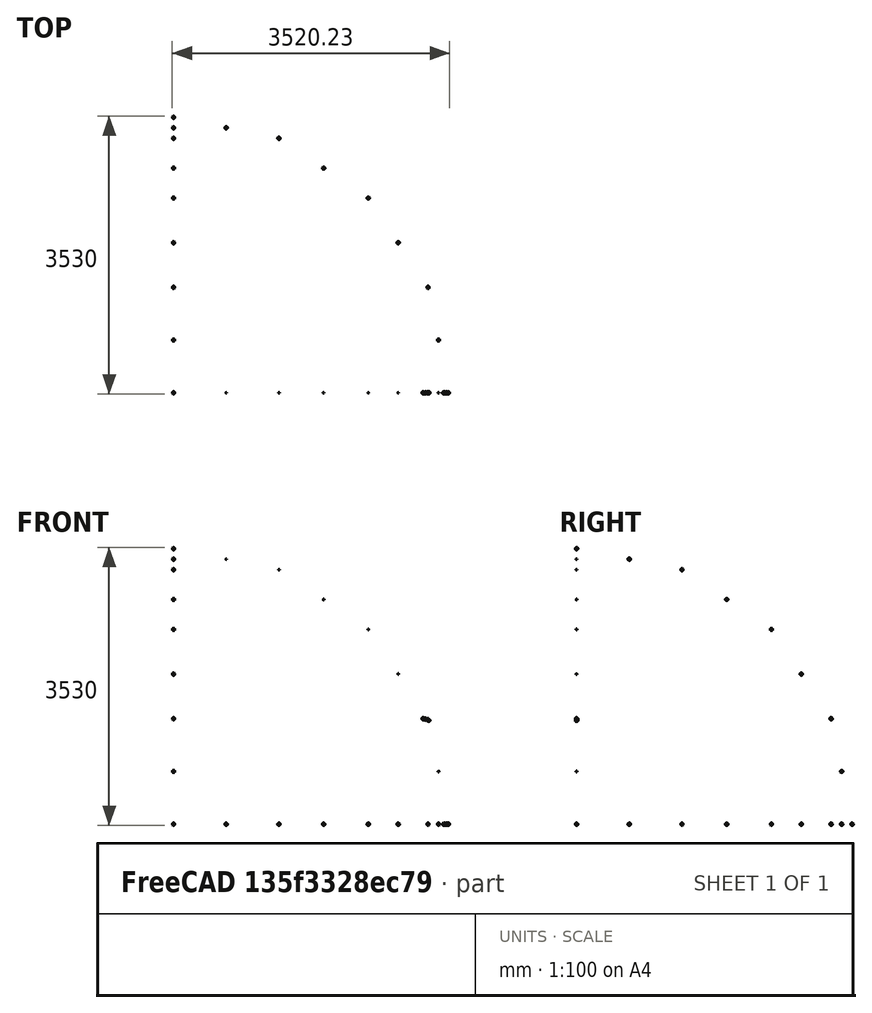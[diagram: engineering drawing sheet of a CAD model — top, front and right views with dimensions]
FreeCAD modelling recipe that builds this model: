
FCSTD DOCUMENT  (FreeCAD 0.20R29603 (Git))
Label: f_pointing
License: All rights reserved
LicenseURL: http://en.wikipedia.org/wiki/All_rights_reserved
objects: Part::Sphere×33, Part::Part2DObjectPython×29, Part::RuledSurface×4
note: 66 computed .brp shape members not serialized (recipe doc carries the construction recipe); baked Part::Feature solids carry a one-line shape summary decoded from their .brp

FEATURE [Part::Part2DObjectPython] Line  # Draft 2D object (typed FeaturePython)
  Area = 0
  ChamferSize = 0
  Closed = false
  End = (3233.58,0,1339.39)
  FilletRadius = 0
  Length = 1365.63
  MakeFace = false
  Points = (2) [(3500,0,0),(3233.58,0,1339.39)]
  Start = (3500,0,0)
  Subdivisions = 0
FEATURE [Part::Part2DObjectPython] Line002  # Draft 2D object (typed FeaturePython)
  Area = 0
  ChamferSize = 0
  Closed = false
  End = (3233.58,1339.39,0)
  FilletRadius = 0
  Length = 1365.63
  MakeFace = false
  Points = (2) [(3500,0,0),(3233.58,1339.39,0)]
  Start = (3500,0,0)
  Subdivisions = 0
FEATURE [Part::Part2DObjectPython] Line003  # Draft 2D object (typed FeaturePython)
  Area = 0
  ChamferSize = 0
  Closed = false
  End = (3171.45,630.84,1339.39)
  FilletRadius = 0
  Length = 1261.68
  MakeFace = false
  Placement = pos=(0,0,0) rot=(0,0,-1;0.19635rad)
  Points = (2) [(3233.58,0,1339.39),(2987.44,1237.44,1339.39)]
  Start = (3171.45,-630.84,1339.39)
  Subdivisions = 0
FEATURE [Part::Part2DObjectPython] Line006  # Draft 2D object (typed FeaturePython)
  Area = 0
  ChamferSize = 0
  Closed = false
  End = (0.0092388,0.00382683,3500)
  FilletRadius = 0
  Length = 0.00390181
  MakeFace = false
  Points = (2) [(0.01,0,3500),(0.0092388,0.00382683,3500)]
  Start = (0.01,0,3500)
  Subdivisions = 0
FEATURE [Part::Part2DObjectPython] Line007  # Draft 2D object (typed FeaturePython)
  Area = 0
  ChamferSize = 0
  Closed = false
  End = (2474.87,0,2474.87)
  FilletRadius = 0
  Length = 1365.63
  MakeFace = false
  Placement = pos=(0,0,0) rot=(0,-1,0;0.392699rad)
  Points = (2) [(3500,0,2.27374e-13),(3233.58,0,1339.39)]
  Start = (3233.58,0,1339.39)
  Subdivisions = 0
FEATURE [Part::Part2DObjectPython] Line008  # Draft 2D object (typed FeaturePython)
  Area = 0
  ChamferSize = 0
  Closed = false
  End = (-1.3642e-12,0,3500)
  FilletRadius = 0
  Length = 1365.63
  MakeFace = false
  Placement = pos=(0,0,0) rot=(0,-1,0;1.1781rad)
  Points = (2) [(3500,0,-4.54747e-13),(3233.58,0,1339.39)]
  Start = (1339.39,0,3233.58)
  Subdivisions = 0
FEATURE [Part::Part2DObjectPython] Line009  # Draft 2D object (typed FeaturePython)
  Area = 0
  ChamferSize = 0
  Closed = false
  End = (1339.39,0,3233.58)
  FilletRadius = 0
  Length = 1365.63
  MakeFace = false
  Placement = pos=(0,0,0) rot=(0,-1,0;0.785398rad)
  Points = (2) [(3500,0,-9.09495e-13),(3233.58,0,1339.39)]
  Start = (2474.87,0,2474.87)
  Subdivisions = 0
FEATURE [Part::Part2DObjectPython] Line010  # Draft 2D object (typed FeaturePython)
  Area = 0
  ChamferSize = 0
  Closed = false
  End = (-1.7053e-12,-2.5011e-12,3500)
  FilletRadius = 0
  Length = 3500
  MakeFace = true
  Placement = pos=(0,0,0) rot=(0.799257,0.125953,0.587643;1.11975rad)
  Points = (2) [(0,0,0),(530.542,2663.76,2207.47)]
  Start = (0,0,0)
  Subdivisions = 0
FEATURE [Part::Part2DObjectPython] Line011  # Draft 2D object (typed FeaturePython)
  Area = 0
  ChamferSize = 0
  Closed = false
  End = (3500,-6.821e-13,0)
  FilletRadius = 0
  Length = 3500
  MakeFace = true
  Placement = pos=(0,0,0) rot=(0.799257,0.125953,0.587643;1.11975rad)
  Points = (2) [(0,0,0),(2786.9,-1652.3,1324.04)]
  Start = (0,0,0)
  Subdivisions = 0
FEATURE [Part::Part2DObjectPython] Line012  # Draft 2D object (typed FeaturePython)
  Area = 0
  ChamferSize = 0
  Closed = false
  End = (2474.87,2474.87,0)
  FilletRadius = 0
  Length = 1365.63
  MakeFace = false
  Placement = pos=(0,0,0) rot=(0,0,1;0.392699rad)
  Points = (2) [(3500,0,0),(3233.58,1339.39,0)]
  Start = (3233.58,1339.39,0)
  Subdivisions = 0
FEATURE [Part::Part2DObjectPython] Line013  # Draft 2D object (typed FeaturePython)
  Area = 0
  ChamferSize = 0
  Closed = false
  End = (1339.39,3233.58,0)
  FilletRadius = 0
  Length = 1365.63
  MakeFace = false
  Placement = pos=(0,0,0) rot=(0,0,1;0.785398rad)
  Points = (2) [(3500,0,0),(3233.58,1339.39,0)]
  Start = (2474.87,2474.87,0)
  Subdivisions = 0
FEATURE [Part::Part2DObjectPython] Line014  # Draft 2D object (typed FeaturePython)
  Area = 0
  ChamferSize = 0
  Closed = false
  End = (-3.4106e-12,3500,0)
  FilletRadius = 0
  Length = 1365.63
  MakeFace = false
  Placement = pos=(0,0,0) rot=(0,0,1;1.1781rad)
  Points = (2) [(3500,0,0),(3233.58,1339.39,0)]
  Start = (1339.39,3233.58,0)
  Subdivisions = 0
FEATURE [Part::Part2DObjectPython] Line015  # Draft 2D object (typed FeaturePython)
  Area = 0
  ChamferSize = 0
  Closed = false
  End = (-6.1391e-12,3500,-1.5348e-12)
  FilletRadius = 0
  Length = 3500
  MakeFace = true
  Placement = pos=(0,0,0) rot=(0.23465,0.959688,0.154721;0.514623rad)
  Points = (2) [(0,0,0),(368.626,3464.19,-336.926)]
  Start = (0,0,0)
  Subdivisions = 0
FEATURE [Part::Part2DObjectPython] Line016  # Draft 2D object (typed FeaturePython)
  Area = 0
  ChamferSize = 0
  Closed = false
  End = (-1.334e-12,-9.095e-13,3500)
  FilletRadius = 0
  Length = 1365.63
  MakeFace = false
  Placement = pos=(0,0,0) rot=(0.485653,-0.485653,0.726831;1.88458rad)
  Points = (2) [(3500,2.66162e-13,-9.09495e-13),(3233.58,-2.59867e-14,1339.39)]
  Start = (-4.5711e-12,1339.39,3233.58)
  Subdivisions = 0
FEATURE [Part::Part2DObjectPython] Line017  # Draft 2D object (typed FeaturePython)
  Area = 0
  ChamferSize = 0
  Closed = false
  End = (-2.261e-12,1339.39,3233.58)
  FilletRadius = 0
  Length = 1365.63
  MakeFace = false
  Placement = pos=(0,0,0) rot=(0.357407,-0.357407,0.862856;1.71777rad)
  Points = (2) [(3500,1.6026e-13,1.81899e-12),(3233.58,1.30286e-13,1339.39)]
  Start = (-3.3201e-12,2474.87,2474.87)
  Subdivisions = 0
FEATURE [Part::Part2DObjectPython] Line018  # Draft 2D object (typed FeaturePython)
  Area = 0
  ChamferSize = 0
  Closed = false
  End = (-5.3986e-12,2474.87,2474.87)
  FilletRadius = 0
  Length = 1365.63
  MakeFace = false
  Placement = pos=(0,0,0) rot=(0.19148,-0.19148,0.962637;1.60887rad)
  Points = (2) [(3500,1.24079e-13,2.27374e-13),(3233.58,1.09381e-13,1339.39)]
  Start = (-6.9822e-12,3233.58,1339.39)
  Subdivisions = 0
FEATURE [Part::Part2DObjectPython] Line019  # Draft 2D object (typed FeaturePython)
  Area = 0
  ChamferSize = 0
  Closed = false
  End = (-3.59e-12,3233.58,1339.39)
  FilletRadius = 0
  Length = 1365.63
  MakeFace = false
  Placement = pos=(0,0,0) rot=(0,0,1;1.5708rad)
  Points = (2) [(3500,0,0),(3233.58,0,1339.39)]
  Start = (-3.8858e-12,3500,0)
  Subdivisions = 0
FEATURE [Part::Sphere] Sphere  label="Сфера"
  Angle1 = -90
  Angle2 = 90
  Angle3 = 360
  AttacherType = Attacher::AttachEngine3D
  Placement = pos=(3500,0,0) rot=(0,0,1;0rad)
  Radius = 5
FEATURE [Part::Sphere] Sphere001  label="Сфера001"
  Angle1 = -90
  Angle2 = 90
  Angle3 = 360
  AttacherType = Attacher::AttachEngine3D
  Radius = 15
FEATURE [Part::Sphere] Sphere002  label="Сфера002"
  Angle1 = -90
  Angle2 = 90
  Angle3 = 360
  AttacherType = Attacher::AttachEngine3D
  Placement = pos=(-1.1369e-12,-1.3642e-12,3500) rot=(0,0,1;0rad)
  Radius = 15
FEATURE [Part::Sphere] Sphere003  label="Сфера003"
  Angle1 = -90
  Angle2 = 90
  Angle3 = 360
  AttacherType = Attacher::AttachEngine3D
  Placement = pos=(1339.39,-1.3642e-12,3233.58) rot=(0,0,1;0rad)
  Radius = 5
FEATURE [Part::Sphere] Sphere004  label="Сфера004"
  Angle1 = -90
  Angle2 = 90
  Angle3 = 360
  AttacherType = Attacher::AttachEngine3D
  Placement = pos=(2474.87,-1.3642e-12,2474.87) rot=(0,0,1;0rad)
  Radius = 5
FEATURE [Part::Sphere] Sphere005  label="Сфера005"
  Angle1 = -90
  Angle2 = 90
  Angle3 = 360
  AttacherType = Attacher::AttachEngine3D
  Placement = pos=(3233.58,-1.3642e-12,1339.39) rot=(0,0,1;0rad)
  Radius = 5
FEATURE [Part::Sphere] Sphere006  label="Сфера006"
  Angle1 = -90
  Angle2 = 90
  Angle3 = 360
  AttacherType = Attacher::AttachEngine3D
  Placement = pos=(4.547e-12,3500,3.183e-12) rot=(0,0,1;0rad)
  Radius = 15
FEATURE [Part::Sphere] Sphere007  label="Сфера007"
  Angle1 = -90
  Angle2 = 90
  Angle3 = 360
  AttacherType = Attacher::AttachEngine3D
  Placement = pos=(4.9019e-12,3233.58,1339.39) rot=(0,0,1;0rad)
  Radius = 15
FEATURE [Part::Sphere] Sphere008  label="Сфера008"
  Angle1 = -90
  Angle2 = 90
  Angle3 = 360
  AttacherType = Attacher::AttachEngine3D
  Placement = pos=(6.1161e-12,2474.87,2474.87) rot=(0,0,1;0rad)
  Radius = 15
FEATURE [Part::Sphere] Sphere009  label="Сфера009"
  Angle1 = -90
  Angle2 = 90
  Angle3 = 360
  AttacherType = Attacher::AttachEngine3D
  Placement = pos=(8.746e-12,1339.39,3233.58) rot=(0,0,1;0rad)
  Radius = 15
FEATURE [Part::Sphere] Sphere010  label="Сфера010"
  Angle1 = -90
  Angle2 = 90
  Angle3 = 360
  AttacherType = Attacher::AttachEngine3D
  Placement = pos=(1339.39,3233.58,-2.728e-12) rot=(0,0,1;0rad)
  Radius = 15
FEATURE [Part::Sphere] Sphere011  label="Сфера011"
  Angle1 = -90
  Angle2 = 90
  Angle3 = 360
  AttacherType = Attacher::AttachEngine3D
  Placement = pos=(2474.87,2474.87,-2.728e-12) rot=(0,0,1;0rad)
  Radius = 15
FEATURE [Part::Sphere] Sphere012  label="Сфера012"
  Angle1 = -90
  Angle2 = 90
  Angle3 = 360
  AttacherType = Attacher::AttachEngine3D
  Placement = pos=(3233.58,1339.39,-2.728e-12) rot=(0,0,1;0rad)
  Radius = 15
FEATURE [Part::Sphere] Sphere013  label="Сфера013"
  Angle1 = -90
  Angle2 = 90
  Angle3 = 360
  AttacherType = Attacher::AttachEngine3D
  Placement = pos=(3366.79,669.696,0) rot=(0,0,1;0rad)
  Radius = 15
FEATURE [Part::Sphere] Sphere014  label="Сфера014"
  Angle1 = -90
  Angle2 = 90
  Angle3 = 360
  AttacherType = Attacher::AttachEngine3D
  Placement = pos=(2854.23,1907.13,0) rot=(0,0,1;0rad)
  Radius = 15
FEATURE [Part::Sphere] Sphere015  label="Сфера015"
  Angle1 = -90
  Angle2 = 90
  Angle3 = 360
  AttacherType = Attacher::AttachEngine3D
  Placement = pos=(1907.13,2854.23,0) rot=(0,0,1;0rad)
  Radius = 15
FEATURE [Part::Sphere] Sphere016  label="Сфера016"
  Angle1 = -90
  Angle2 = 90
  Angle3 = 360
  AttacherType = Attacher::AttachEngine3D
  Placement = pos=(669.696,3366.79,0) rot=(0,0,1;0rad)
  Radius = 15
FEATURE [Part::Sphere] Sphere017  label="Сфера017"
  Angle1 = -90
  Angle2 = 90
  Angle3 = 360
  AttacherType = Attacher::AttachEngine3D
  Placement = pos=(-4.3201e-12,3366.79,669.696) rot=(0,0,1;0rad)
  Radius = 15
FEATURE [Part::Sphere] Sphere018  label="Сфера018"
  Angle1 = -90
  Angle2 = 90
  Angle3 = 360
  AttacherType = Attacher::AttachEngine3D
  Placement = pos=(-4.664e-12,2854.23,1907.13) rot=(0,0,1;0rad)
  Radius = 15
FEATURE [Part::Sphere] Sphere019  label="Сфера019"
  Angle1 = -90
  Angle2 = 90
  Angle3 = 360
  AttacherType = Attacher::AttachEngine3D
  Placement = pos=(-2.188e-12,1907.13,2854.23) rot=(0,0,1;0rad)
  Radius = 15
FEATURE [Part::Sphere] Sphere020  label="Сфера020"
  Angle1 = -90
  Angle2 = 90
  Angle3 = 360
  AttacherType = Attacher::AttachEngine3D
  Placement = pos=(-1.925e-12,669.696,3366.79) rot=(0,0,1;0rad)
  Radius = 15
FEATURE [Part::Sphere] Sphere021  label="Сфера021"
  Angle1 = -90
  Angle2 = 90
  Angle3 = 360
  AttacherType = Attacher::AttachEngine3D
  Placement = pos=(669.696,-1.14e-13,3366.79) rot=(0,0,1;0rad)
  Radius = 5
FEATURE [Part::Sphere] Sphere022  label="Сфера022"
  Angle1 = -90
  Angle2 = 90
  Angle3 = 360
  AttacherType = Attacher::AttachEngine3D
  Placement = pos=(1907.13,-1.14e-13,2854.23) rot=(0,0,1;0rad)
  Radius = 5
FEATURE [Part::Sphere] Sphere023  label="Сфера023"
  Angle1 = -90
  Angle2 = 90
  Angle3 = 360
  AttacherType = Attacher::AttachEngine3D
  Placement = pos=(2854.23,-1.14e-13,1907.13) rot=(0,0,1;0rad)
  Radius = 5
FEATURE [Part::Sphere] Sphere024  label="Сфера024"
  Angle1 = -90
  Angle2 = 90
  Angle3 = 360
  AttacherType = Attacher::AttachEngine3D
  Placement = pos=(3366.79,-1.14e-13,669.696) rot=(0,0,1;0rad)
  Radius = 5
FEATURE [Part::Part2DObjectPython] Line020  # Draft 2D object (typed FeaturePython)
  Area = 0
  ChamferSize = 0
  Closed = false
  End = (3432.75,682.816,0)
  FilletRadius = 0
  Length = 1365.63
  MakeFace = false
  Placement = pos=(0,0,0) rot=(0,0,-1;0.19635rad)
  Points = (2) [(3500,0,0),(3233.58,1339.39,0)]
  Start = (3432.75,-682.816,0)
  Subdivisions = 0
FEATURE [Part::Part2DObjectPython] Line023  # Draft 2D object (typed FeaturePython)
  Area = 0
  ChamferSize = 0
  Closed = false
  End = (1313.66,9.633e-13,3233.58)
  FilletRadius = 0
  Length = 1325.4
  MakeFace = true
  Placement = pos=(3245.45,-1.3105e-12,1302.6) rot=(-0.303013,-0.887024,0.348384;4.06875rad)
  Points = (2) [(-463.604,-2843.01,-2637.38),(-820.808,-1855.95,-1828.18)]
  Start = (14.7118,-1.9926e-12,3497.07)
  Subdivisions = 0
FEATURE [Part::Part2DObjectPython] Line025  # Draft 2D object (typed FeaturePython)
  Area = 0
  ChamferSize = 0
  Closed = false
  End = (3466.54,1.9328e-12,-2.5011e-12)
  FilletRadius = 0
  Length = 1347.55
  MakeFace = true
  Placement = pos=(3228.4,6.254e-13,1326.34) rot=(-0.404939,-0.858628,0.314296;4.40953rad)
  Points = (2) [(0,0,0),(1285.82,130.976,381.305)]
  Start = (3228.4,6.254e-13,1326.34)
  Subdivisions = 0
FEATURE [Part::Part2DObjectPython] Line027  # Draft 2D object (typed FeaturePython)
  Area = 0
  ChamferSize = 0
  Closed = false
  End = (3442.68,1.8451e-12,-5.0022e-12)
  FilletRadius = 0
  Length = 1357.59
  MakeFace = true
  Placement = pos=(3198.94,1.1736e-12,1335.53) rot=(-0.530052,-0.805781,0.264125;4.73974rad)
  Points = (2) [(0,0,0),(1330.87,-265.566,35.9882)]
  Start = (3198.94,1.1736e-12,1335.53)
  Subdivisions = 0
FEATURE [Part::Part2DObjectPython] Line029  # Draft 2D object (typed FeaturePython)
  Area = 0
  ChamferSize = 0
  Closed = false
  End = (3432.75,3.0128e-12,-2.0464e-12)
  FilletRadius = 0
  Length = 1364.64
  MakeFace = true
  Placement = pos=(3171.45,1.478e-12,1339.39) rot=(0.686613,0.703228,-0.184481;1.23965rad)
  Points = (2) [(0,0,0),(1173.31,-621.678,-314.807)]
  Start = (3171.45,1.4779e-12,1339.39)
  Subdivisions = 0
FEATURE [Part::Sphere] Sphere025  label="Сфера025"
  Angle1 = -90
  Angle2 = 90
  Angle3 = 360
  AttacherType = Attacher::AttachEngine3D
  Placement = pos=(3466.54,1.0797e-12,-9.095e-13) rot=(0,-1,0;5.48809rad)
  Radius = 15
FEATURE [Part::Sphere] Sphere026  label="Сфера026"
  Angle1 = -90
  Angle2 = 90
  Angle3 = 360
  AttacherType = Attacher::AttachEngine3D
  Placement = pos=(3442.68,1.4204e-12,-2.7285e-12) rot=(0,-1,0;5.88358rad)
  Radius = 15
FEATURE [Part::Sphere] Sphere027  label="Сфера027"
  Angle1 = -90
  Angle2 = 90
  Angle3 = 360
  AttacherType = Attacher::AttachEngine3D
  Placement = pos=(3171.45,1.4772e-12,1339.39) rot=(0,0,1;0rad)
  Radius = 15
FEATURE [Part::Sphere] Sphere028  label="Сфера028"
  Angle1 = -90
  Angle2 = 90
  Angle3 = 360
  AttacherType = Attacher::AttachEngine3D
  Placement = pos=(3432.75,-1.91e-13,0) rot=(0,0,1;0rad)
  Radius = 15
FEATURE [Part::RuledSurface] Ruled_Surface003
  Curve1 = -> Line003 [Edge1]
  Curve2 = -> Line020 [Edge1]
  Orientation = 0
FEATURE [Part::Part2DObjectPython] Line004  # Draft 2D object (typed FeaturePython)
  Area = 0
  ChamferSize = 0
  Closed = false
  End = (2427.32,482.824,2474.87)
  FilletRadius = 0
  Length = 965.648
  MakeFace = false
  Placement = pos=(0,0,0) rot=(0,0,-1;0.19635rad)
  Points = (2) [(2474.87,-1.7053e-13,2474.87),(2286.49,947.093,2474.87)]
  Start = (2427.32,-482.824,2474.87)
  Subdivisions = 0
FEATURE [Part::RuledSurface] Ruled_Surface002
  Curve1 = -> Line004 [Edge1]
  Curve2 = -> Line003 [Edge1]
  Orientation = 0
  Placement = pos=(0,0,0) rot=(0,-1,0;5.88358rad)
FEATURE [Part::Part2DObjectPython] Line005  # Draft 2D object (typed FeaturePython)
  Area = 0
  ChamferSize = 0
  Closed = false
  End = (1313.66,261.302,3233.58)
  FilletRadius = 0
  Length = 522.605
  MakeFace = false
  Placement = pos=(0,0,0) rot=(0,0,-1;0.19635rad)
  Points = (2) [(1339.39,-1.13687e-13,3233.58),(1237.44,512.563,3233.58)]
  Start = (1313.66,-261.302,3233.58)
  Subdivisions = 0
FEATURE [Part::RuledSurface] Ruled_Surface001
  Curve1 = -> Line005 [Edge1]
  Curve2 = -> Line004 [Edge1]
  Orientation = 0
  Placement = pos=(0,0,0) rot=(0,-1,0;5.48809rad)
FEATURE [Part::Part2DObjectPython] Line037  # Draft 2D object (typed FeaturePython)
  Area = 0
  ChamferSize = 0
  Closed = false
  End = (1313.66,261.302,3233.58)
  FilletRadius = 0
  Length = 1365.63
  MakeFace = true
  Placement = pos=(-1.4779e-12,-2.2737e-12,3500) rot=(0.914982,0.176951,0.362624;1.15387rad)
  Points = (2) [(0,0,0),(1288.71,-431.374,134.535)]
  Start = (-1.4779e-12,-2.2737e-12,3500)
  Subdivisions = 0
FEATURE [Part::Part2DObjectPython] Line036  # Draft 2D object (typed FeaturePython)
  Area = 0
  ChamferSize = 0
  Closed = false
  End = (1313.66,-261.302,3233.58)
  FilletRadius = 0
  Length = 1365.63
  MakeFace = true
  Placement = pos=(-1.4779e-12,-2.2737e-12,3500) rot=(0.914982,0.176951,0.362624;1.15387rad)
  Points = (2) [(0,0,0),(1065.08,-652.742,551.793)]
  Start = (-1.4779e-12,-2.2737e-12,3500)
  Subdivisions = 0
FEATURE [Part::RuledSurface] Ruled_Surface
  Curve1 = -> Line036 [Edge1]
  Curve2 = -> Line037 [Edge1]
  Orientation = 0
  Placement = pos=(0,0,0) rot=(0,-1,0;5.09828rad)
FEATURE [Part::Sphere] Sphere029  label="Сфера029"
  Angle1 = -90
  Angle2 = 90
  Angle3 = 360
  AttacherType = Attacher::AttachEngine3D
  Placement = pos=(3242.63,-2.1035e-12,1317.33) rot=(0,1,0;0.795098rad)
  Radius = 15
FEATURE [Part::Sphere] Sphere030  label="Сфера030"
  Angle1 = -90
  Angle2 = 90
  Angle3 = 360
  AttacherType = Attacher::AttachEngine3D
  Placement = pos=(3490.23,5.686e-13,-2.9559e-12) rot=(0,1,0;0.795098rad)
  Radius = 15
FEATURE [Part::Sphere] Sphere031  label="Сфера031"
  Angle1 = -90
  Angle2 = 90
  Angle3 = 360
  AttacherType = Attacher::AttachEngine3D
  Placement = pos=(3198.94,1.1926e-12,1335.53) rot=(0,1,0;0.399606rad)
  Radius = 15
FEATURE [Part::Sphere] Sphere032  label="Сфера032"
  Angle1 = -90
  Angle2 = 90
  Angle3 = 360
  AttacherType = Attacher::AttachEngine3D
  Placement = pos=(3228.4,6.255e-13,1326.34) rot=(0,1,0;0.795098rad)
  Radius = 15
FEATURE [Part::Part2DObjectPython] Line038  # Draft 2D object (typed FeaturePython)
  Area = 0
  ChamferSize = 0
  Closed = false
  End = (3171.45,1.478e-12,-1.3642e-12)
  FilletRadius = 0
  Length = 1339.39
  MakeFace = true
  Placement = pos=(3171.45,1.478e-12,1339.39) rot=(1,0,0;1.5708rad)
  Points = (2) [(0,0,0),(0,-1339.39,-2.97405e-13)]
  Start = (3171.45,1.478e-12,1339.39)
  Subdivisions = 0
FEATURE [Part::Part2DObjectPython] Line039  # Draft 2D object (typed FeaturePython)
  Area = 0
  ChamferSize = 0
  Closed = false
  End = (3306.88,-2.063e-13,645.188)
  FilletRadius = 0
  Length = 3369.23
  MakeFace = true
  Placement = pos=(0,0,0) rot=(1,0,0;1.5708rad)
  Points = (2) [(0,0,0),(3306.88,645.188,3.49566e-13)]
  Start = (0,0,0)
  Subdivisions = 0
FEATURE [Part::Part2DObjectPython] Line040  # Draft 2D object (typed FeaturePython)
  Area = 0
  ChamferSize = 0
  Closed = false
  End = (3306.88,-2.063e-13,0)
  FilletRadius = 0
  Length = 645.188
  MakeFace = true
  Placement = pos=(3306.88,-2.063e-13,645.188) rot=(1,0,0;1.5708rad)
  Points = (2) [(0,0,0),(0,-645.188,-1.43261e-13)]
  Start = (3306.88,-2.063e-13,645.188)
  Subdivisions = 0
